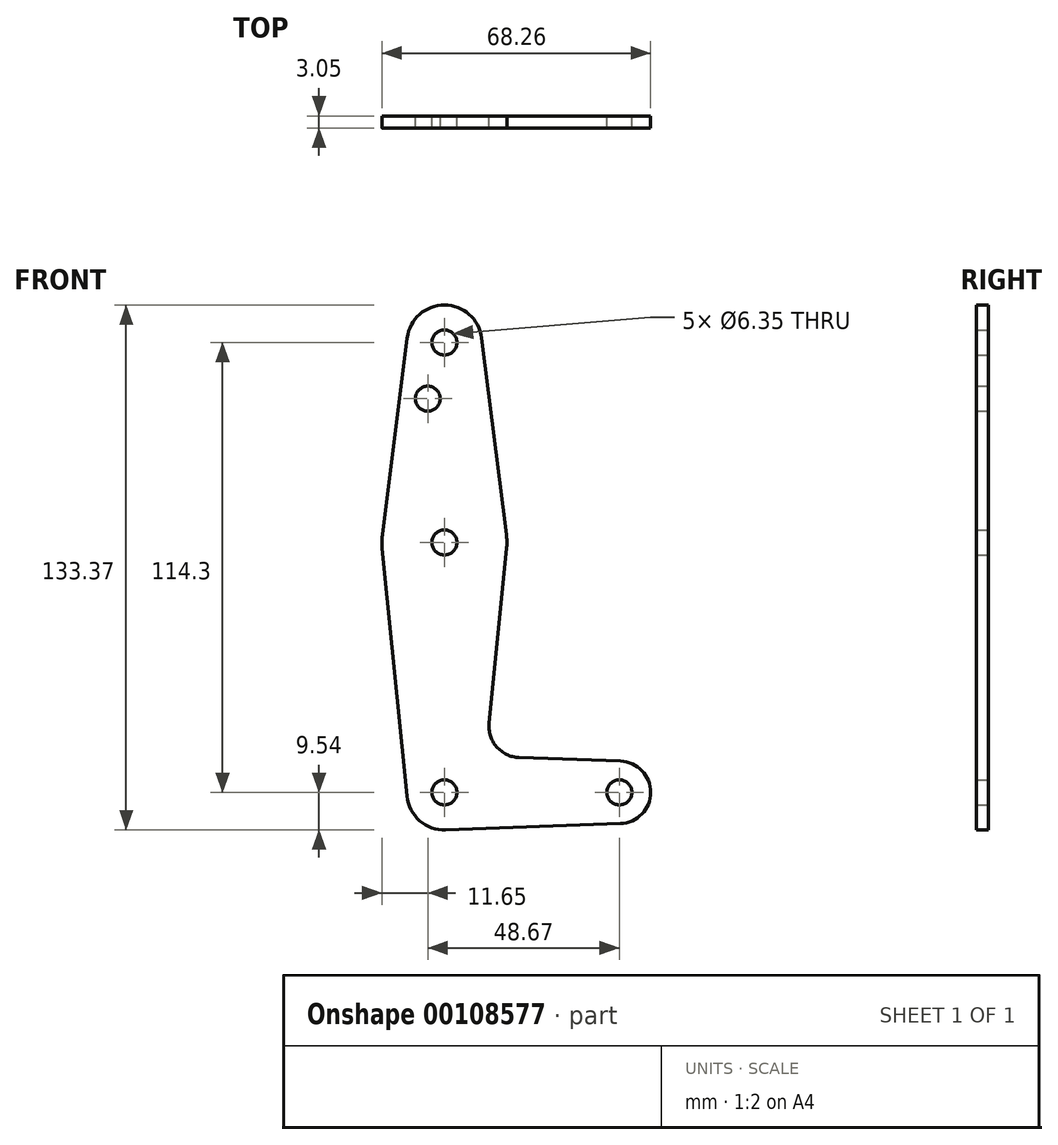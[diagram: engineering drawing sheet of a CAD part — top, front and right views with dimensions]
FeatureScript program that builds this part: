
annotation { "Feature Type Name" : "Feature", "Feature Type Description" : "" }
export const myFeature = defineFeature(function(context is Context, id is Id, definition is map)
    precondition{}
    {
        {
            var Q0;
            Q0=qCreatedBy(makeId("Front.planeOp"),FACE);
            var sketch = newSketch(context, id + "F0", { "sketchPlane" : qUnion([Q0])});
            skLineSegment(sketch, "E0", {"start": v(0, 0) * mm, "end": v(0, 3.18) * mm});
            skLineSegment(sketch, "E1", {"start": v(0, 63.5) * mm, "end": v(0, 114.3) * mm});
            skCircle(sketch, "E2", {"center": v(0, 0) * mm, "radius": 9.54 * mm});
            skCircle(sketch, "E3", {"center": v(0, 63.5) * mm, "radius": 15.88 * mm});
            skCircle(sketch, "E4", {"center": v(0, 114.3) * mm, "radius": 9.53 * mm});
            skLineSegment(sketch, "E5", {"start": v(0, 0) * mm, "end": v(3.18, 0) * mm});
            skCircle(sketch, "E6", {"center": v(44.45, 0) * mm, "radius": 7.94 * mm});
            skLineSegment(sketch, "E7", {"start": v(-9.45, 115.5) * mm, "end": v(-15.75, 65.48) * mm});
            skLineSegment(sketch, "E8", {"start": v(-15.8, 61.92) * mm, "end": v(-9.49, -0.95) * mm});
            skLineSegment(sketch, "E9", {"start": v(9.45, 115.5) * mm, "end": v(15.75, 65.48) * mm});
            skLineSegment(sketch, "E10", {"start": v(15.8, 61.92) * mm, "end": v(11.35, 17.6) * mm});
            skLineSegment(sketch, "E11", {"start": v(0.34, -9.53) * mm, "end": v(44.74, -7.93) * mm});
            skLineSegment(sketch, "E12", {"start": v(18.97, 8.86) * mm, "end": v(44.74, 7.93) * mm});
            skCircle(sketch, "E13", {"center": v(0, 114.3) * mm, "radius": 3.18 * mm});
            skCircle(sketch, "E14", {"center": v(0, 63.5) * mm, "radius": 3.18 * mm});
            skCircle(sketch, "E15", {"center": v(0, 0) * mm, "radius": 3.18 * mm});
            skCircle(sketch, "E16", {"center": v(44.45, 0) * mm, "radius": 3.18 * mm});
            skCircle(sketch, "E17", {"center": v(-4.22, 100.03) * mm, "radius": 3.18 * mm});
            skArc(sketch, "E18.filletArc", {"start": v(11.35, 17.6) * mm, "mid": v(13.27, 11.58) * mm, "end": v(18.97, 8.86) * mm});
            skLineSegment(sketch, "E19.trimOffspring", {"start": v(9.54, 0) * mm, "end": v(44.45, 0) * mm});
            skLineSegment(sketch, "E20.trimOffspring", {"start": v(0, 9.54) * mm, "end": v(0, 63.5) * mm});
            skSolve(sketch);
        }
        {
            var Q0;
            Q0 = qSketchRegion(id + "F0", true);
            extrude(context, id + "F1", {"entities" : qUnion([Q0]), "depth" : 3.05 * mm});
        }
    });
